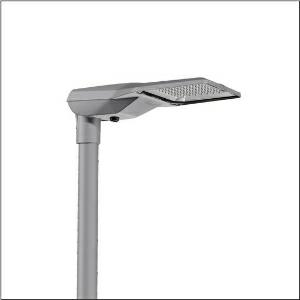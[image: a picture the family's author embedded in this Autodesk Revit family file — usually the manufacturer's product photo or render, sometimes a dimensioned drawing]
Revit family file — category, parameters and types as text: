
# Revit family: streetlight_sl_21_midi___p0_8ab_5xe3r33r08nb_8880
name_source: partatom
category: Lighting Fixtures
units: mm (PartAtom-declared; Revit-internal decimal feet)

## family parameters
Cut with Voids When Loaded = No
Host = Face
Light Source = No
Part Type = Normal
Room Calculation Point = No
Round Connector Dimension = Use Diameter
Shared = No

## types (1)
- --- (1 x LED, 19710 lm, 151.2 W, 3000K)
    Apparent Load = 151 VA
    CIE Flux Codes = 39 72 97 100 100
    Color Rendering = 70
    Color Temperature = 3000K
    Default Elevation = 1800 mm
    Description = Streetlight SL 21 midi, mast luminaire, primary light control with lens, of PMMA, primary optical cover: cover, of toughened safety glass, transparent, light distribution: P0.8aB, light emission: direct distribution, primary light characteristic: asymmetric, installation type: post-top, side-entry, LED, High Power LED, rated luminous flux: 19.710lm, luminous efficacy: 130lm/W, light colour: 730, colour temperature: 3000K, control gear: D4i, control: pre-setting: logarithmic dimming characteristic, flexible luminous flux parameterisation, time-dependent luminous flux control, constant luminous flux control, overheat protection, mains connection: 230..240V, AC, 50/60Hz, start of lifetime: 151W, end of service life: 157W, reduction: 70W, luminaire housing, of diecast aluminium, powder-coated, Siteco® metallic grey (DB 702S), corrosivity category C5 mid according to DIN EN ISO 12944, multi-level sealing system, sealing non-destructively replaceable, inclination adjustable: 0°, 5°, 10°, 15°, please order mast flange separately, length: 644mm, width: 335mm, height: 110mm, mast flange for spigot size: 42mm (side-entry): 5XC10008XM4, 60/48mm (side-entry/post-top): 5XC10108XM2, 76/60mm (side-entry/post-top): 5XC10108XM1, mounting height: 4..8m, Smart Interface below, protection rating (complete): IP66, insulation class (complete): insulation class II (safety insulation), certification: CE, ENEC, ENEC+, VDE, impact resistance: IK10, permissible operating ambient temperature for outdoor applications: -40..+50°C, standard-compliant lighting for roads and squares, packaging unit: 1 piece

Light Distribution: P0.8aB
    Height = 111 mm
    Lamp = 1 x LED
    Lamp Light Flux = 19710 lm
    Lamp Power = 151.2 W
    Lamp count = 1
    Length = 644 mm
    Luminous efficacy = 130 lm/W
    Manufacturer = Siteco
    ModVariant = No
    Model = 5XE3R33R08NB
    Number of Poles = 1
    OnlyDefault = Yes
    Power Factor = 1
    Product Name = Streetlight SL 21 midi | P0.8aB
    Product group = mast luminaire | pylon top
    ProductGroupID = 6100
    Protection Class = Protection class II
    Protection Degree = IP 66
    RLX_Detail_Level = 1
    RLX_Emergency_Light_Flux = 0 lm
    RLX_Emergency_Type = 0
    RLX_Emergency_Type_DB = No
    RlxData = <blob elided: 90045 chars, md5=8f5b4f33>
    Socket = socket
    Standby Power = 0 W
    System Light Flux = 19710 lm
    System Power = 151 W
    Type Comments = factory setting: luminous flux: 100 % | dim-lin: 254 | 802 mA
    Type Image = l_1004300.jpg
    URL = http://relux.com
    VarID = @adj_092503
    Voltage = 0 V
    Weight = 0.00 kg
    Width = 336 mm

## geometry (parser evidence)
native form markers: Blend x4, Sweep x11
no freeform markers — native parametric forms only
